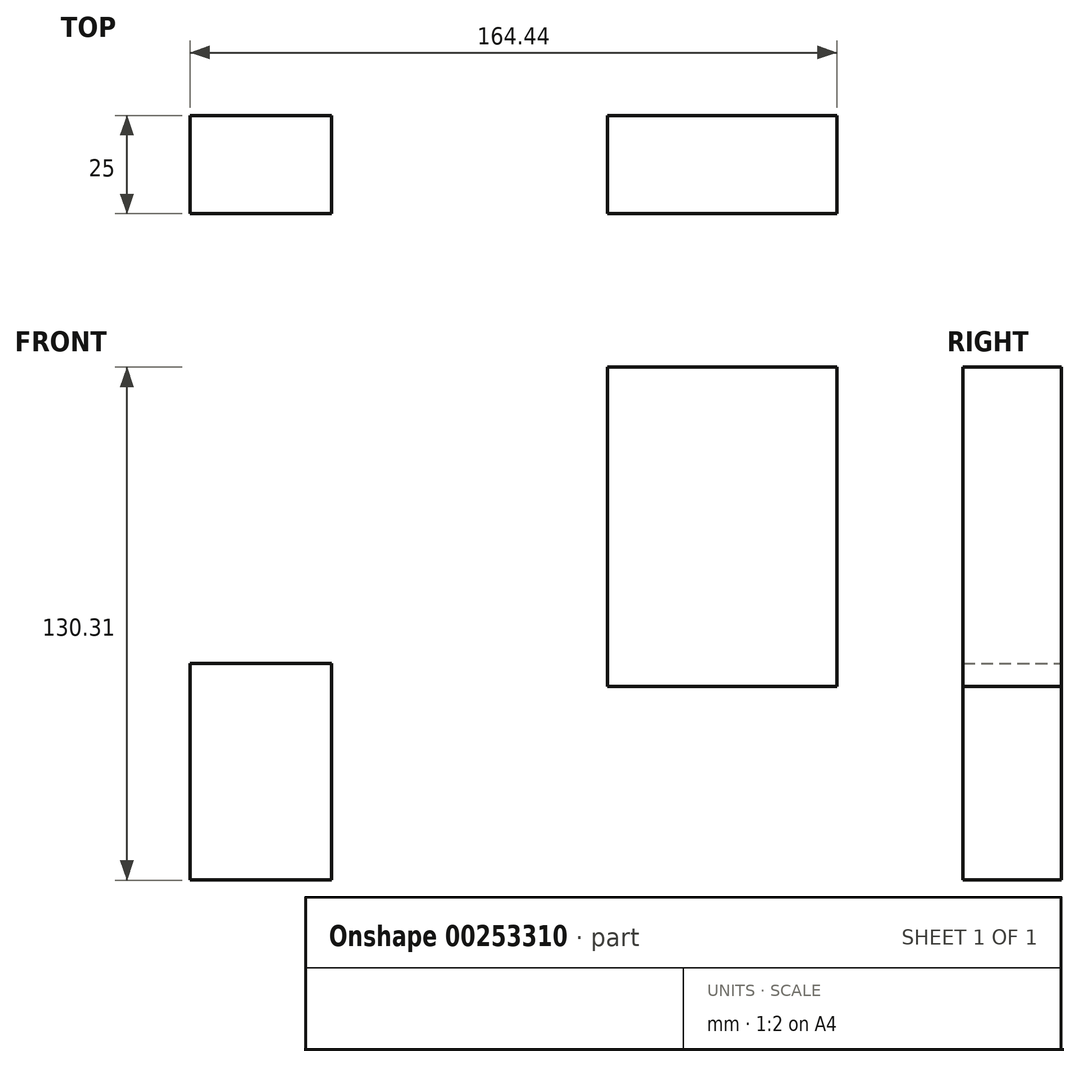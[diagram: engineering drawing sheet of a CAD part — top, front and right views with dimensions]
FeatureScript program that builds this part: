
annotation { "Feature Type Name" : "Feature", "Feature Type Description" : "" }
export const myFeature = defineFeature(function(context is Context, id is Id, definition is map)
    precondition{}
    {
        {
            var Q0;
            Q0=qCreatedBy(makeId("Front.planeOp"),FACE);
            var sketch = newSketch(context, id + "F0", { "sketchPlane" : qUnion([Q0])});
            skLineSegment(sketch, "E0.bottom", {"start": v(-264.68, -36.44) * mm, "end": v(-228.65, -36.44) * mm});
            skLineSegment(sketch, "E0.top", {"start": v(-264.68, -91.56) * mm, "end": v(-228.65, -91.56) * mm});
            skLineSegment(sketch, "E0.left", {"start": v(-264.68, -36.44) * mm, "end": v(-264.68, -91.56) * mm});
            skLineSegment(sketch, "E0.right", {"start": v(-228.65, -36.44) * mm, "end": v(-228.65, -91.56) * mm});
            skLineSegment(sketch, "E1.bottom", {"start": v(-158.55, 38.75) * mm, "end": v(-100.24, 38.75) * mm});
            skLineSegment(sketch, "E1.top", {"start": v(-158.55, -42.37) * mm, "end": v(-100.24, -42.37) * mm});
            skLineSegment(sketch, "E1.left", {"start": v(-158.55, 38.75) * mm, "end": v(-158.55, -42.37) * mm});
            skLineSegment(sketch, "E1.right", {"start": v(-100.24, 38.75) * mm, "end": v(-100.24, -42.37) * mm});
            skSolve(sketch);
        }
        {
            var Q0;
            Q0 = qSketchRegion(id + "F0", true);
            extrude(context, id + "F1", {"entities" : qUnion([Q0]), "depth" : 25 * mm});
        }
    });
